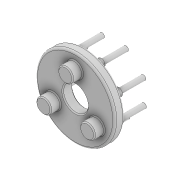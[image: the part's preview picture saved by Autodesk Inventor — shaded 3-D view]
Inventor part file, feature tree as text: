
AUTODESK INVENTOR PART (.ipt)
format: ipt  version: 2020.3 (Build 243373010, 373A)  size: 231,936 bytes
history: native  units: mm
features: sketch x5, extrude x5, fillet x3, chamfer x3, pattern_circular x2, projected_geometry x1
ambient origin geometry x8: Origin, YZ Plane, XZ Plane, XY Plane, X Axis, Y Axis, Z Axis, Center Point
bodies: Solid1 (feature_tree)
feature tree (19):
  sketch  "Sketch1"  dims[d0=80.0mm d1=30.0mm d2=0.0mm]
  extrude  "Extrusion1"  Depth=30.0mm TaperAngle=0.0deg
  extrude  "Extrusion2"  Depth=8.0mm
  sketch  "Sketch2"  dims[d3=10.0mm d4=0.0mm d8=8.0mm]
  extrude  "Extrusion3"  Depth=5.0mm TaperAngle=360.0deg
  pattern_circular  "Circular Pattern1"  Angle=45.0deg  [1 undecoded]
  fillet  "Fillet1"  Radius=25.0mm
  fillet  "Fillet2"  [1 undecoded]
  chamfer  "Chamfer2"  Distance=76.0mm
  extrude  "Extrusion4"  Depth=25.0mm
  extrude  "Extrusion5"  Depth=2.0mm
  fillet  "Fillet3"  Radius=15.0mm
  chamfer  "Chamfer3"  Distance=10.0mm
  pattern_circular  "Circular Pattern2"  [2 undecoded]
  chamfer  "Chamfer4"  Distance=1.0mm Angle=45.0deg
  sketch  "Sketch3"  dims[d9=5.0mm d10=0.0mm d11=80.0mm d12=360.0deg]
  sketch  "Sketch4"  dims[d14=2.0mm]
  sketch  "Sketch5"  dims[d15=2.0mm d16=0.5mm d17=2.0mm d18=45.0deg d19=25.0mm d20=0.0mm d21=0.0mm d22=76.0mm d23=25.0mm d24=25.5mm d25=15.0mm d26=10.0mm d27=0.0mm d28=1.0mm d29=1.0mm d30=2.0mm d31=45.0deg d32=30.0mm d33=360.0deg d35=1.0mm d36=2.0mm d37=45.0deg]
  projected_geometry  "Projected Loop1"
note: 4 required parameter values undecoded (feature->parameter linkage not recoverable at this tier; creation-order binding heuristic only, values carry confidence <= 0.55)
